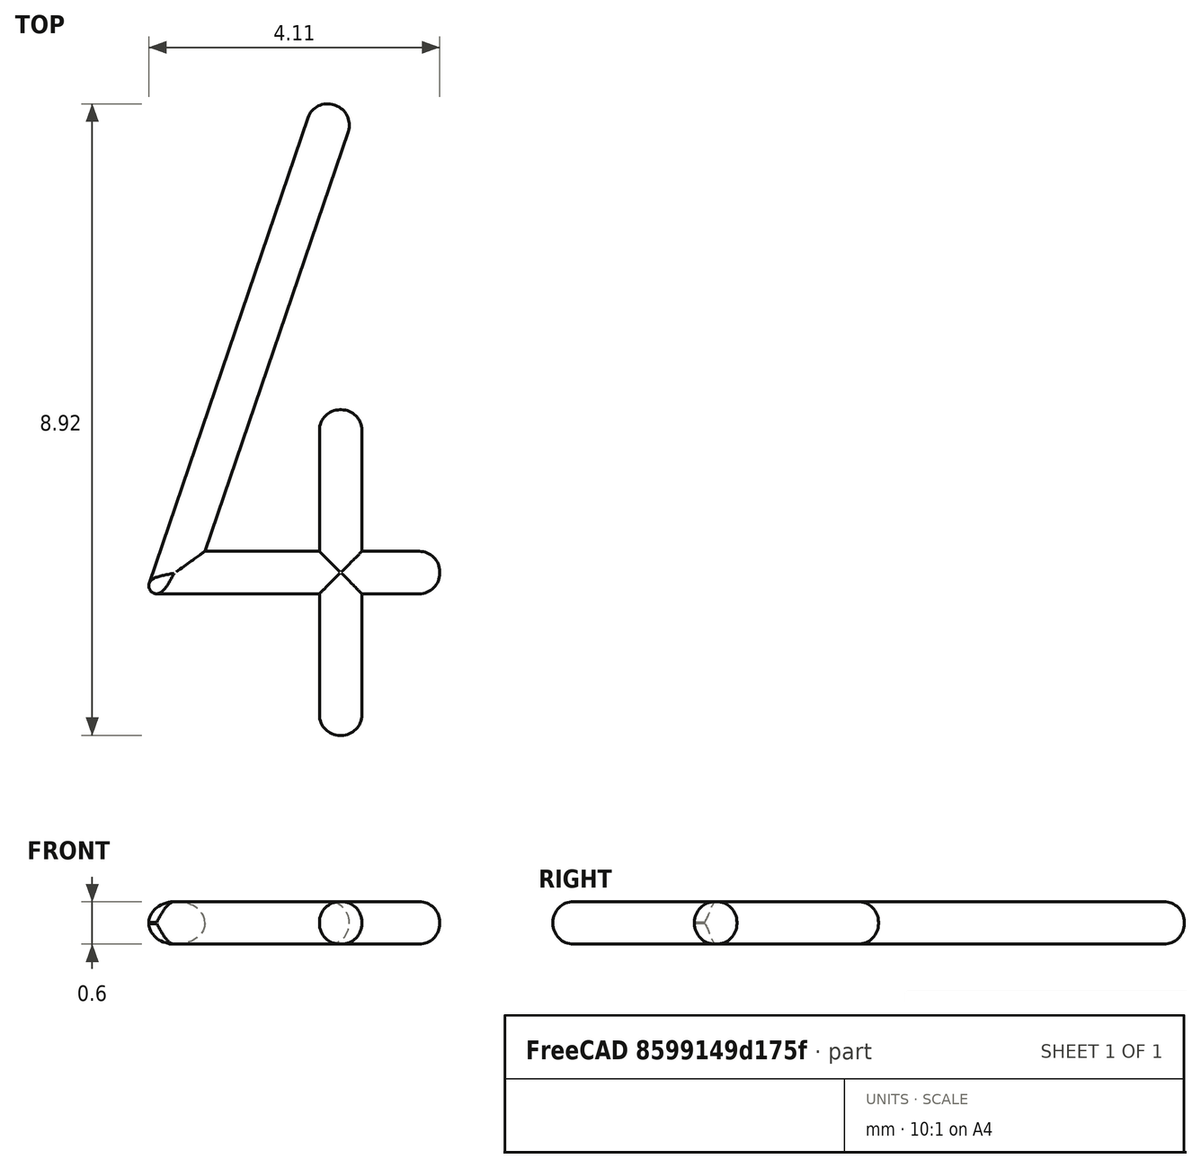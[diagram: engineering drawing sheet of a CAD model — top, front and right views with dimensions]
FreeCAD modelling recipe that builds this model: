
FCSTD DOCUMENT  (FreeCAD 0.16R6712 (Git))
Label: 4s
License: All rights reserved
LicenseURL: http://en.wikipedia.org/wiki/All_rights_reserved
objects: Sketcher::SketchObject×1, PartDesign::Pad×1, PartDesign::Fillet×1, Mesh::Feature×1
note: 4 computed .brp shape members not serialized (recipe doc carries the construction recipe); baked Part::Feature solids carry a one-line shape summary decoded from their .brp

FEATURE [Sketcher::SketchObject] Sketch
  sketch-geometry (15):
    g0: LineSegment StartX=0.232178 StartY=9 StartZ=0 EndX=-2.10627 EndY=2.15033 EndZ=0
    g1: LineSegment StartX=0.8 StartY=8.80615 StartZ=0 EndX=-1.31875 EndY=2.6 EndZ=0
    g2: LineSegment StartX=-1.99875 StartY=2 StartZ=0 EndX=0.3 EndY=2 EndZ=0
    g3: LineSegment StartX=-1.31875 StartY=2.6 StartZ=0 EndX=0.3 EndY=2.6 EndZ=0
    g4: LineSegment StartX=0.232178 StartY=9 StartZ=0 EndX=0.8 EndY=8.80615 EndZ=0
    g5: LineSegment StartX=0.3 StartY=4.6 StartZ=0 EndX=0.9 EndY=4.6 EndZ=0
    g6: LineSegment StartX=0.9 StartY=4.6 StartZ=0 EndX=0.9 EndY=2.6 EndZ=0
    g7: LineSegment StartX=0.9 StartY=0 StartZ=0 EndX=0.3 EndY=0 EndZ=0
    g8: LineSegment StartX=0.3 StartY=0 StartZ=0 EndX=0.3 EndY=2 EndZ=0
    g9: LineSegment StartX=0.9 StartY=2 StartZ=0 EndX=0.9 EndY=0 EndZ=0
    g10: LineSegment StartX=0.3 StartY=2.6 StartZ=0 EndX=0.3 EndY=4.6 EndZ=0
    g11: LineSegment StartX=0.9 StartY=2.6 StartZ=0 EndX=2 EndY=2.6 EndZ=0
    g12: LineSegment StartX=0.9 StartY=2 StartZ=0 EndX=2 EndY=2 EndZ=0
    g13: LineSegment StartX=2 StartY=2.6 StartZ=0 EndX=2 EndY=2 EndZ=0
    g14: ArcOfCircle CenterX=-1.99875 CenterY=2.11362 CenterZ=0 NormalX=0 NormalY=0 NormalZ=1 Radius=0.113619 StartAngle=2.8126 EndAngle=4.71239
  constraints (40):
    c: Horizontal(g2)
    c: Horizontal(g3)
    c: Coincident(g4,g1)
    c: Coincident(g1,g3)
    c: Perpendicular(g1,g4)
    c: Coincident(g0,g4)
    c: Distance(g0,g1) = 0.6
    c: Distance(g11,g12) = 0.6
    c: Parallel(g0,g1)
    c: Coincident(g5,g6)
    c: Coincident(g9,g7)
    c: Coincident(g7,g8)
    c: Coincident(g10,g5)
    c: Horizontal(g5)
    c: Horizontal(g7)
    c: Vertical(g6)
    c: Vertical(g8)
    c: Coincident(g3,g10)
    c: Coincident(g11,g6)
    c: Tangent(g3,g11)
    c: Coincident(g2,g8)
    c: Coincident(g12,g9)
    c: Tangent(g2,g12)
    c: Distance(g6,g5) = 2
    c: Coincident(g13,g11)
    c: Coincident(g13,g12)
    c: Vertical(g13)
    c: PointOnObject(g7,g-1)
    c: Distance(g7,g12) = 2
    c: DistanceY(g-1,g0) = 9
    c: DistanceX(g-2,g1) = 0.8
    c: Tangent(g0,g14) = -1.5708
    c: Tangent(g2,g14) = -1.5708
    c: DistanceX(g-2,g12) = 2
    c: Distance(g11,g6) = 1.1
    c: Distance(g12,g9) = 1.1
    c: Vertical(g9)
    c: DistanceX(g5,g5) = 0.6
    c: DistanceX(g7,g7) = 0.6
    c: Vertical(g10)
FEATURE [PartDesign::Pad] Pad
  Length = 0.6
  Length2 = 100
  Midplane = true
  Sketch = -> Sketch
  Type = 0
FEATURE [PartDesign::Fillet] Fillet
  Base = -> Pad [Edge4,Edge7,Edge10,Edge13,Edge16,Edge19,Edge22,Edge25,Edge28,Edge31,Edge34,Edge37,Edge40,Edge43,Edge45,Edge3,Edge6,Edge9,Edge12,Edge15,Edge18,Edge21,Edge24,Edge27,Edge30,Edge33,Edge36,Edge39,Edge42,Edge44,Edge26,Edge23,Edge35,Edge32,Edge1,Edge2,Edge17,Edge14]
  Radius = 0.29
FEATURE [Mesh::Feature] Mesh  label="Fillet (Meshed)"
